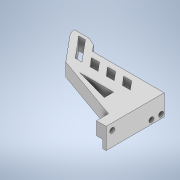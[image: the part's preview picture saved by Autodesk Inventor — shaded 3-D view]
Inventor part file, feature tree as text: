
AUTODESK INVENTOR PART (.ipt)
format: ipt  version: 2021 (Build 250183000, 183)  size: 346,624 bytes
history: native  units: mm
features: extrude x18, sketch x18, chamfer x2, other x1, fillet x1
ambient origin geometry x8: Origin, YZ Plane, XZ Plane, XY Plane, X Axis, Y Axis, Z Axis, Center Point
bodies: Body1 (feature_tree)
feature tree (40):
  other  "Sólido1"
  extrude  "Extrusión1"  Depth=6.0mm
  extrude  "Extrusión2"  Depth=8.0mm TaperAngle=0.0deg
  extrude  "Extrusión3"  Depth=4.0mm TaperAngle=0.0deg
  extrude  "Extrusión4"  Depth=8.0mm TaperAngle=0.0deg
  extrude  "Extrusión5"  Depth=2.0mm
  extrude  "Extrusión6"  Depth=3.0mm
  extrude  "Extrusión7"  Depth=3.0mm TaperAngle=0.0deg
  extrude  "Extrusión8"  Depth=5.0mm TaperAngle=0.0deg
  fillet  "Empalme1"  Radius=5.0mm
  chamfer  "Chaflán1"  Distance=10.0mm
  extrude  "Extrusión9"  Depth=8.0mm TaperAngle=0.0deg
  extrude  "Extrusión10"  Depth=2.0mm TaperAngle=45.0deg
  extrude  "Extrusión11"  Depth=6.0mm
  extrude  "Extrusión13"  Depth=4.0mm TaperAngle=0.0deg
  extrude  "Extrusión14"  Depth=12.0mm
  extrude  "Extrusión15"  Depth=2.0mm
  extrude  "Extrusión16"  Depth=2.0mm
  extrude  "Extrusión17"  Depth=9.0mm
  extrude  "Extrusión18"  Depth=3.0mm
  extrude  "Extrusión19"  Depth=2.0mm TaperAngle=0.0deg
  chamfer  "Chaflán2"  Distance=2.0mm
  sketch  "Boceto1"  dims[d1=6.0mm d8=6.0mm]
  sketch  "Boceto2"  dims[d9=0.5mm d10=8.0mm d11=0.0mm]
  sketch  "Boceto3"  dims[d12=6.0mm d13=4.0mm d14=0.0mm]
  sketch  "Boceto4"  dims[d15=5.0mm d16=8.0mm d17=0.0mm]
  sketch  "Boceto5"  dims[d18=5.0mm d19=2.0mm]
  sketch  "Boceto6"  dims[d20=2.0mm d21=3.0mm]
  sketch  "Boceto7"  dims[d22=3.0mm d23=3.0mm d24=0.0mm]
  sketch  "Boceto8"  dims[d25=3.0mm d26=5.0mm d27=0.0mm d28=5.0mm]
  sketch  "Boceto9"  dims[d29=5.0mm]
  sketch  "Boceto10"  dims[d30=5.0mm]
  sketch  "Boceto12"  dims[d31=5.0mm]
  sketch  "Boceto14"  dims[d32=5.0mm]
  sketch  "Boceto15"  dims[d33=5.0mm]
  sketch  "Boceto16"  dims[d34=5.0mm]
  sketch  "Boceto17"  dims[d35=5.0mm]
  sketch  "Boceto19"  dims[d36=5.0mm d37=10.0mm d38=0.0mm]
  sketch  "Boceto20"  dims[d39=10.0mm d40=0.0mm d41=8.0mm d42=0.0mm]
  sketch  "Boceto21"  dims[d43=2.0mm d44=2.0mm d45=2.0mm d46=45.0deg d47=6.0mm d48=4.0mm d49=0.0mm d50=12.0mm d51=19.0mm d52=4.5mm d53=9.0mm d54=3.0mm d55=2.0mm d56=0.0mm d57=2.0mm d58=20.0mm d59=5.0mm d60=5.0mm d61=5.0mm d62=8.0mm d63=0.0mm d64=5.0mm d68=8.0mm d69=0.0mm d70=8.0mm d71=0.0mm d72=5.0mm d73=5.0mm d74=5.0mm d75=5.0mm d76=5.0mm d77=5.0mm d78=5.0mm d79=5.0mm d80=8.0mm d81=0.0mm d82=2.0mm d83=0.0mm d84=4.0mm d85=6.0mm d86=13.0mm d87=0.0mm d88=13.0mm d89=0.0mm d90=3.0mm d91=13.0mm d92=0.0mm d93=1.0mm d94=2.0mm d95=45.0deg]
